# Revit family: Deca_Cabide Clean_2060.C.CLN
name_source: partatom
category: Plumbing Fixtures
revit_build: Autodesk Revit 2013 (Build: 20120221_2030(x64)
units: mm (PartAtom-declared; Revit-internal decimal feet)

## types (1)
- 2060.C.CLN_Cromado CR10
    Acabamento = Deca CR10 Cromado
    Aprovado por = Contino/quattroD
    Assembly Code = D2010
    Atendimento ao Cliente = 0800-0117073
    Criado por = Contino/quattroD
    Código = 2060.C.CLN
    Default Elevation = 2000 mm  [stored 6.56168 ft]
    Description = Cabide
    HWFU = 0
    Informações Complementares = Os parafusos e buchas que acompanham o produto devem ser utilzados apenas em paredes de concreto ou tijolo maciço. Para instalações em Drywall, consultar projetista ou engenheiro da obra
    Linha = Clean
    Louça/Metais = Metal
    Manufacturer = Deca
    Material = Deca_Latão Cromado e Plástico de Engenharia
    Model = 2060.C.CLN
    Norma = ABNT NBR 10283: 2003
    Peso Liquido (Kg) = 0.11
    Produto = Cabide Clean
    Segmento = Medio
    URL = www.deca.com.br/produtos
    Variações de COR = Cromado (2060.C.CLN)

note: [stored X ft] marks values corroborated as IEEE doubles in the binary element streams (Revit-internal decimal feet)

## geometry (parser evidence)
native form markers: Blend x6, Sweep x2
no freeform markers — native parametric forms only
